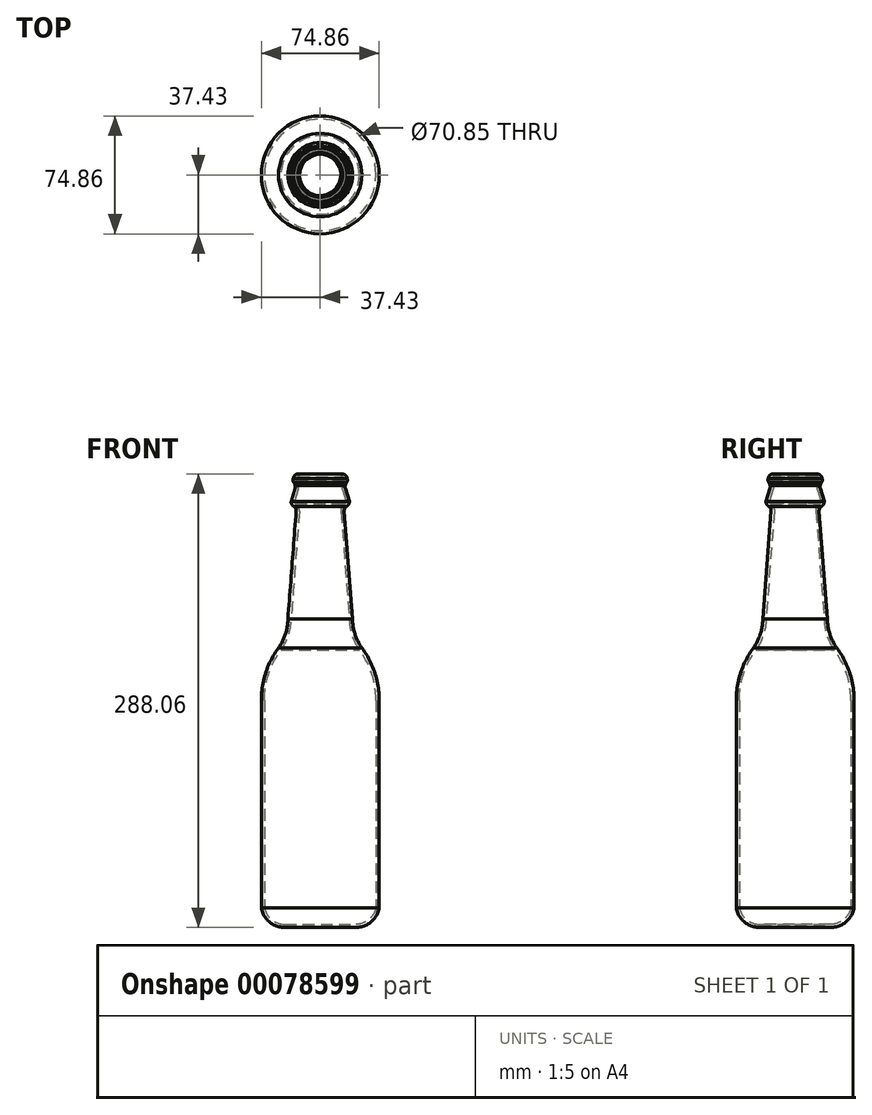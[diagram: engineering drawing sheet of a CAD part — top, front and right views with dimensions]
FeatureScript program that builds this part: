
annotation { "Feature Type Name" : "Feature", "Feature Type Description" : "" }
export const myFeature = defineFeature(function(context is Context, id is Id, definition is map)
    precondition{}
    {
        {
            var Q0;
            Q0=qCreatedBy(makeId("Front.planeOp"),FACE);
            var sketch = newSketch(context, id + "F0", { "sketchPlane" : qUnion([Q0])});
            skLineSegment(sketch, "E0", {"start": v(0, 1.69) * mm, "end": v(-22.61, 1.69) * mm});
            skArc(sketch, "E1", {"start": v(-37.43, 14.18) * mm, "mid": v(-32.3, 5.23) * mm, "end": v(-22.61, 1.69) * mm});
            skLineSegment(sketch, "E2", {"start": v(-37.43, 14.18) * mm, "end": v(-37.43, 146.04) * mm});
            skArc(sketch, "E3", {"start": v(-26.52, 179.16) * mm, "mid": v(-34.63, 163.48) * mm, "end": v(-37.43, 146.04) * mm});
            skArc(sketch, "E4", {"start": v(-26.52, 179.16) * mm, "mid": v(-22.1, 187.97) * mm, "end": v(-20.52, 197.7) * mm});
            skLineSegment(sketch, "E5", {"start": v(-20.52, 197.7) * mm, "end": v(-15.24, 266.18) * mm});
            skArc(sketch, "E6", {"start": v(-15.24, 266.18) * mm, "mid": v(-15.59, 267.9) * mm, "end": v(-16.78, 269.2) * mm});
            skArc(sketch, "E7", {"start": v(-18.47, 272.26) * mm, "mid": v(-18.06, 270.49) * mm, "end": v(-16.78, 269.2) * mm});
            skLineSegment(sketch, "E8", {"start": v(-18.47, 272.26) * mm, "end": v(-15.97, 280.47) * mm});
            skArc(sketch, "E9", {"start": v(-15.97, 280.47) * mm, "mid": v(-15.82, 281.51) * mm, "end": v(-15.97, 282.56) * mm});
            skArc(sketch, "E10", {"start": v(-15.97, 282.56) * mm, "mid": v(-16.26, 283.53) * mm, "end": v(-16.78, 284.4) * mm});
            skArc(sketch, "E11", {"start": v(-17.1, 286.99) * mm, "mid": v(-17.24, 285.66) * mm, "end": v(-16.78, 284.4) * mm});
            skArc(sketch, "E12", {"start": v(-14.16, 289.75) * mm, "mid": v(-16.14, 288.9) * mm, "end": v(-17.1, 286.99) * mm});
            skArc(sketch, "E13.0", {"start": v(-14.07, 287.75) * mm, "mid": v(-14.85, 287.36) * mm, "end": v(-15.1, 286.52) * mm});
            skArc(sketch, "E13.1", {"start": v(-15.1, 286.52) * mm, "mid": v(-15.26, 286.04) * mm, "end": v(-15.14, 285.56) * mm});
            skArc(sketch, "E13.2", {"start": v(-14.02, 283) * mm, "mid": v(-14.43, 284.35) * mm, "end": v(-15.14, 285.56) * mm});
            skArc(sketch, "E13.3", {"start": v(-24.9, 177.99) * mm, "mid": v(-32.73, 162.86) * mm, "end": v(-35.43, 146.04) * mm});
            skLineSegment(sketch, "E13.4", {"start": v(-35.43, 14.36) * mm, "end": v(-35.43, 146.04) * mm});
            skArc(sketch, "E13.5", {"start": v(-35.43, 14.36) * mm, "mid": v(-30.95, 6.7) * mm, "end": v(-22.61, 3.69) * mm});
            skLineSegment(sketch, "E13.6", {"start": v(0, 3.69) * mm, "end": v(-22.61, 3.69) * mm});
            skArc(sketch, "E13.7", {"start": v(-24.9, 177.99) * mm, "mid": v(-20.2, 187.3) * mm, "end": v(-18.52, 197.61) * mm});
            skLineSegment(sketch, "E13.8", {"start": v(-18.52, 197.61) * mm, "end": v(-13.25, 266.02) * mm});
            skArc(sketch, "E13.9", {"start": v(-13.25, 266.02) * mm, "mid": v(-13.82, 268.84) * mm, "end": v(-15.78, 270.94) * mm});
            skArc(sketch, "E13.10", {"start": v(-16.47, 271.96) * mm, "mid": v(-16.26, 271.36) * mm, "end": v(-15.78, 270.94) * mm});
            skLineSegment(sketch, "E13.11", {"start": v(-16.47, 271.96) * mm, "end": v(-14.06, 279.88) * mm});
            skArc(sketch, "E13.12", {"start": v(-14.06, 279.88) * mm, "mid": v(-13.82, 281.44) * mm, "end": v(-14.02, 283) * mm});
            skLineSegment(sketch, "E14", {"start": v(0, 3.69) * mm, "end": v(0, 1.69) * mm});
            skArc(sketch, "E15", {"start": v(-14.07, 287.75) * mm, "mid": v(-13.17, 288.8) * mm, "end": v(-14.16, 289.75) * mm});
            skLineSegment(sketch, "E16", {"start": v(0, 0) * mm, "end": v(0, 363.63) * mm});
            skSolve(sketch);
        }
        {
            var Q0;
            Q0 = qSketchRegion(id + "F0", true);
            var Q1;
            Q1=sQuery(id+"F0.wireOp",EDGE,"E16");
            revolve(context, id + "F1", {"entities" : qUnion([Q0]), "axis" : qUnion([Q1]), "revolveType" : RevolveType.FULL});
        }
    });
